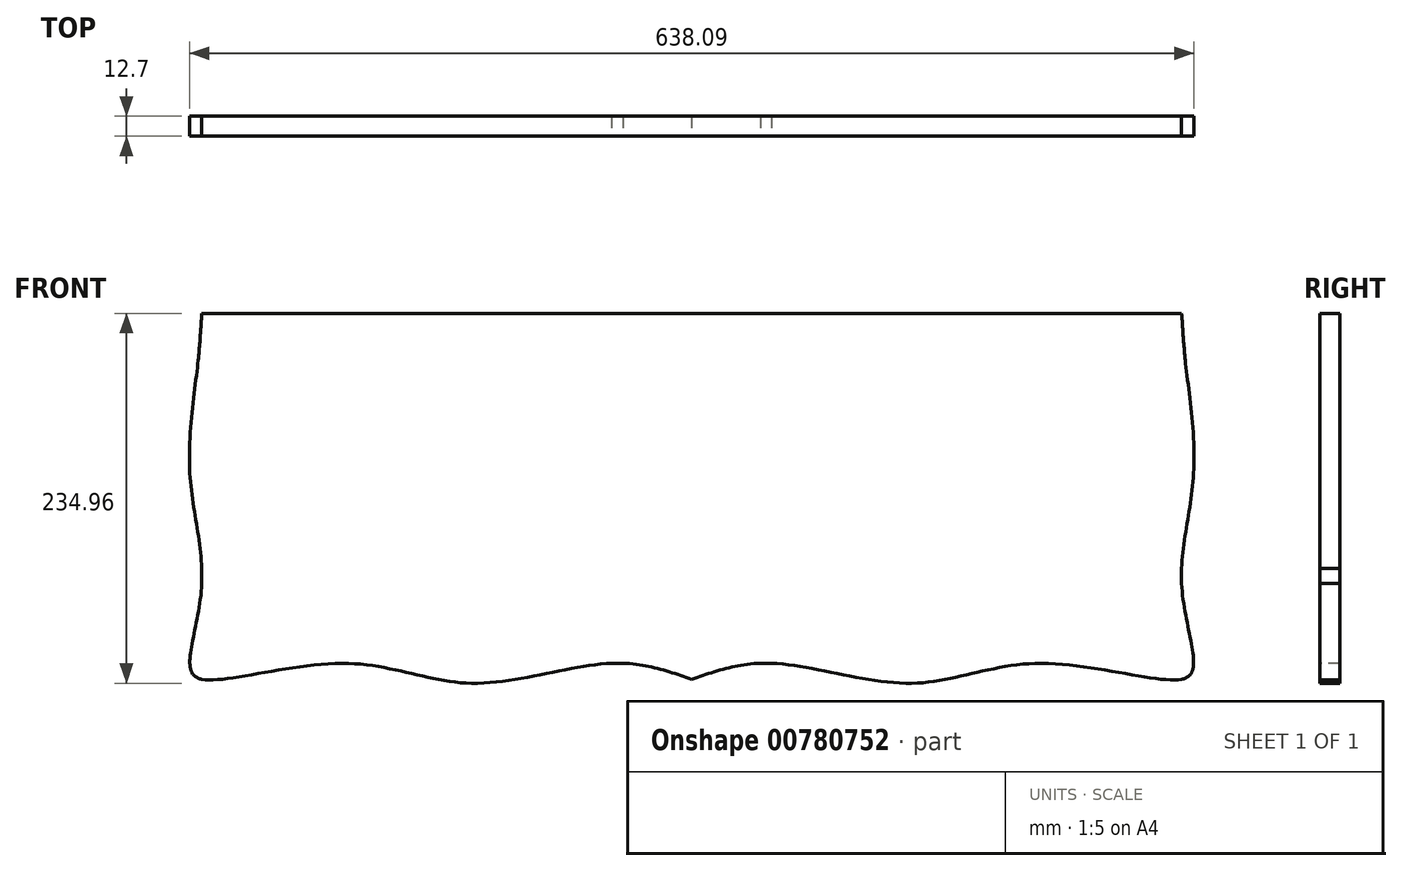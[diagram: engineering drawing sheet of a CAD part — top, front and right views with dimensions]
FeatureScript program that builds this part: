
annotation { "Feature Type Name" : "Feature", "Feature Type Description" : "" }
export const myFeature = defineFeature(function(context is Context, id is Id, definition is map)
    precondition{}
    {
        {
            var Q0;
            Q0=qCreatedBy(makeId("Front.planeOp"),FACE);
            var sketch = newSketch(context, id + "F0", { "sketchPlane" : qUnion([Q0])});
            skLineSegment(sketch, "E0.bottom", {"start": v(-290.57, 108.48) * mm, "end": v(331.73, 108.48) * mm});
            skLineSegment(sketch, "E0.top", {"start": v(-290.57, -113.77) * mm, "end": v(331.73, -113.77) * mm});
            skLineSegment(sketch, "E0.left", {"start": v(-290.57, 108.48) * mm, "end": v(-290.57, -113.77) * mm});
            skLineSegment(sketch, "E0.right", {"start": v(331.73, 108.48) * mm, "end": v(331.73, -113.77) * mm});
            skPoint(sketch, "E1", {"position": v(20.58, 108.48) * mm});
            skSolve(sketch);
        }
        {
            var Q0;
            Q0=makeQuery(id+"F0.imprint","IMPRINT",FACE,{"disambiguationData":[TD([[makeQuery(id+"F0.imprint","IMPRINT",EDGE,{"derivedFrom":sQuery(id+"F0.wireOp",EDGE,"E0.bottom")}),-1.0]])]});
            extrude(context, id + "F1", {"entities" : qUnion([Q0]), "depth" : 12.7 * mm, "offsetDistance" : 25.4 * mm});
        }
        {
            var Q0;
            {var subQ0=sQuery(id+"F0.wireOp",EDGE,"E0.right");var subQ1=sQuery(id+"F0.wireOp",EDGE,"E0.bottom");var subQ2=sQuery(id+"F0.wireOp",EDGE,"E0.left");var subQ3=sQuery(id+"F0.wireOp",EDGE,"E0.top");Q0=makeQuery(id+"FjgwLtvUwF4HY63_1.boolean.opBoolean","SPLIT",FACE,{"disambiguationData":[TD([makeQuery(id+"F1.opExtrude","SWEPT_FACE",FACE,{"disambiguationData":[OSD([subQ1])]})])],"derivedFrom":makeQuery(id+"F1.opExtrude","CAP_FACE",FACE,{"disambiguationData":[OSD([subQ1,subQ3,subQ2,subQ0])],"isStart":false})});}
            var sketch = newSketch(context, id + "F2", { "sketchPlane" : qUnion([Q0])});
            skPoint(sketch, "E2", {"position": v(-290.57, -62.97) * mm});
            skPoint(sketch, "E3", {"position": v(-290.57, 6.88) * mm});
            skPoint(sketch, "E4", {"position": v(-290.57, 76.73) * mm});
            skLineSegment(sketch, "E5", {"start": v(-290.57, 76.73) * mm, "end": v(-293.1, 76.73) * mm});
            skLineSegment(sketch, "E6", {"start": v(-290.57, 6.88) * mm, "end": v(-298.19, 6.88) * mm});
            skLineSegment(sketch, "E7", {"start": v(-290.57, -113.77) * mm, "end": v(-298.19, -113.77) * mm});
            skLineSegment(sketch, "E8", {"start": v(-290.57, -113.77) * mm, "end": v(-290.57, -123.93) * mm});
            skPoint(sketch, "E9", {"position": v(-201.67, -113.77) * mm});
            skPoint(sketch, "E10", {"position": v(20.58, -113.77) * mm});
            skPoint(sketch, "E11", {"position": v(-30.22, -113.77) * mm});
            skPoint(sketch, "E12", {"position": v(-119.12, -113.77) * mm});
            skPoint(sketch, "E13", {"position": v(71.38, -113.77) * mm});
            skPoint(sketch, "E14", {"position": v(160.28, -113.77) * mm});
            skPoint(sketch, "E15", {"position": v(242.83, -113.77) * mm});
            skPoint(sketch, "E16", {"position": v(331.73, -62.97) * mm});
            skPoint(sketch, "E17", {"position": v(331.73, 6.88) * mm});
            skPoint(sketch, "E18", {"position": v(331.73, 76.73) * mm});
            skLineSegment(sketch, "E19", {"start": v(331.73, 76.73) * mm, "end": v(334.27, 76.73) * mm});
            skLineSegment(sketch, "E20", {"start": v(331.73, 6.88) * mm, "end": v(339.35, 6.88) * mm});
            skLineSegment(sketch, "E21", {"start": v(331.73, -113.77) * mm, "end": v(339.35, -113.77) * mm});
            skLineSegment(sketch, "E22", {"start": v(331.73, -113.77) * mm, "end": v(331.73, -123.93) * mm});
            skLineSegment(sketch, "E23", {"start": v(-119.12, -113.77) * mm, "end": v(-119.12, -126.47) * mm});
            skLineSegment(sketch, "E24", {"start": v(20.58, -113.77) * mm, "end": v(20.58, -123.93) * mm});
            skLineSegment(sketch, "E25", {"start": v(160.28, -113.77) * mm, "end": v(160.28, -126.47) * mm});
            skFitSpline(sketch, "E26", {"points": [v(-290.57, 108.48) * mm, v(-293.1, 76.73) * mm, v(-298.19, 6.88) * mm, v(-290.57, -62.97) * mm, v(-298.19, -113.77) * mm, v(-290.57, -123.93) * mm, v(-201.67, -113.77) * mm, v(-119.12, -126.47) * mm, v(-30.22, -113.77) * mm, v(20.58, -123.93) * mm], "startDerivative": vector(-26.2, -341.82) * mm, "endDerivative": vector(438.15, -148.5) * mm});
            skFitSpline(sketch, "E27", {"points": [v(331.73, 108.48) * mm, v(334.27, 76.73) * mm, v(339.35, 6.88) * mm, v(331.73, -62.97) * mm, v(339.35, -113.77) * mm, v(331.73, -123.93) * mm, v(242.83, -113.77) * mm, v(160.28, -126.47) * mm, v(71.38, -113.77) * mm, v(20.58, -123.93) * mm], "startDerivative": vector(26.2, -341.82) * mm, "endDerivative": vector(-438.15, -148.5) * mm});
            skSolve(sketch);
        }
        {
            var Q0;
            {var subQ0=sQuery(id+"F2.wireOp",EDGE,"E24");Q0=makeQuery(id+"F2.imprint","IMPRINT",FACE,{"disambiguationData":[TD([[makeQuery(id+"F2.imprint","IMPRINT",EDGE,{"derivedFrom":subQ0}),-1.0]])]});}
            var Q1;
            {var subQ0=sQuery(id+"F2.wireOp",EDGE,"E24");Q1=makeQuery(id+"F2.imprint","IMPRINT",FACE,{"disambiguationData":[TD([[makeQuery(id+"F2.imprint","IMPRINT",EDGE,{"derivedFrom":subQ0}),1.0]])]});}
            var Q2;
            {var subQ0=sQuery(id+"F2.wireOp",EDGE,"E23");Q2=makeQuery(id+"F2.imprint","IMPRINT",FACE,{"disambiguationData":[TD([[makeQuery(id+"F2.imprint","IMPRINT",EDGE,{"derivedFrom":subQ0}),1.0]])]});}
            var Q3;
            {var subQ0=sQuery(id+"F2.wireOp",EDGE,"E23");Q3=makeQuery(id+"F2.imprint","IMPRINT",FACE,{"disambiguationData":[TD([[makeQuery(id+"F2.imprint","IMPRINT",EDGE,{"derivedFrom":subQ0}),-1.0]])]});}
            var Q4;
            {var subQ0=sQuery(id+"F2.wireOp",EDGE,"E8");Q4=makeQuery(id+"F2.imprint","IMPRINT",FACE,{"disambiguationData":[TD([[makeQuery(id+"F2.imprint","IMPRINT",EDGE,{"derivedFrom":subQ0}),1.0]])]});}
            var Q5;
            {var subQ0=sQuery(id+"F2.wireOp",EDGE,"E7");Q5=makeQuery(id+"F2.imprint","IMPRINT",FACE,{"disambiguationData":[TD([[makeQuery(id+"F2.imprint","IMPRINT",EDGE,{"derivedFrom":subQ0}),1.0]])]});}
            var Q6;
            {var subQ0=sQuery(id+"F2.wireOp",EDGE,"E7");Q6=makeQuery(id+"F2.imprint","IMPRINT",FACE,{"disambiguationData":[TD([[makeQuery(id+"F2.imprint","IMPRINT",EDGE,{"derivedFrom":subQ0}),-1.0]])]});}
            var Q7;
            {var subQ0=sQuery(id+"F2.wireOp",EDGE,"E6");Q7=makeQuery(id+"F2.imprint","IMPRINT",FACE,{"disambiguationData":[TD([[makeQuery(id+"F2.imprint","IMPRINT",EDGE,{"derivedFrom":subQ0}),1.0]])]});}
            var Q8;
            {var subQ0=sQuery(id+"F2.wireOp",EDGE,"E5");Q8=makeQuery(id+"F2.imprint","IMPRINT",FACE,{"disambiguationData":[TD([[makeQuery(id+"F2.imprint","IMPRINT",EDGE,{"derivedFrom":subQ0}),1.0]])]});}
            var Q9;
            {var subQ0=makeQuery(id+"F1.opExtrude","CAP_EDGE",EDGE,{"disambiguationData":[OSD([sQuery(id+"F0.wireOp",EDGE,"E0.bottom")])],"isStart":false});Q9=makeQuery(id+"F2.imprint","IMPRINT",FACE,{"disambiguationData":[TD([[makeQuery(id+"F2.imprint","IMPRINT",EDGE,{"derivedFrom":subQ0}),-1.0]])]});}
            var Q10;
            {var subQ0=sQuery(id+"F2.wireOp",EDGE,"E25");Q10=makeQuery(id+"F2.imprint","IMPRINT",FACE,{"disambiguationData":[TD([[makeQuery(id+"F2.imprint","IMPRINT",EDGE,{"derivedFrom":subQ0}),-1.0]])]});}
            var Q11;
            {var subQ0=sQuery(id+"F2.wireOp",EDGE,"E25");Q11=makeQuery(id+"F2.imprint","IMPRINT",FACE,{"disambiguationData":[TD([[makeQuery(id+"F2.imprint","IMPRINT",EDGE,{"derivedFrom":subQ0}),1.0]])]});}
            var Q12;
            {var subQ0=sQuery(id+"F2.wireOp",EDGE,"E22");Q12=makeQuery(id+"F2.imprint","IMPRINT",FACE,{"disambiguationData":[TD([[makeQuery(id+"F2.imprint","IMPRINT",EDGE,{"derivedFrom":subQ0}),-1.0]])]});}
            var Q13;
            {var subQ0=sQuery(id+"F2.wireOp",EDGE,"E21");Q13=makeQuery(id+"F2.imprint","IMPRINT",FACE,{"disambiguationData":[TD([[makeQuery(id+"F2.imprint","IMPRINT",EDGE,{"derivedFrom":subQ0}),-1.0]])]});}
            var Q14;
            {var subQ0=sQuery(id+"F2.wireOp",EDGE,"E21");Q14=makeQuery(id+"F2.imprint","IMPRINT",FACE,{"disambiguationData":[TD([[makeQuery(id+"F2.imprint","IMPRINT",EDGE,{"derivedFrom":subQ0}),1.0]])]});}
            var Q15;
            {var subQ0=sQuery(id+"F2.wireOp",EDGE,"E20");Q15=makeQuery(id+"F2.imprint","IMPRINT",FACE,{"disambiguationData":[TD([[makeQuery(id+"F2.imprint","IMPRINT",EDGE,{"derivedFrom":subQ0}),-1.0]])]});}
            var Q16;
            {var subQ0=sQuery(id+"F2.wireOp",EDGE,"E19");Q16=makeQuery(id+"F2.imprint","IMPRINT",FACE,{"disambiguationData":[TD([[makeQuery(id+"F2.imprint","IMPRINT",EDGE,{"derivedFrom":subQ0}),-1.0]])]});}
            var Q17;
            {var subQ0=sQuery(id+"F2.wireOp",EDGE,"E19");Q17=makeQuery(id+"F2.imprint","IMPRINT",FACE,{"disambiguationData":[TD([[makeQuery(id+"F2.imprint","IMPRINT",EDGE,{"derivedFrom":subQ0}),1.0]])]});}
            var Q18;
            {var subQ0=sQuery(id+"F2.wireOp",EDGE,"E5");Q18=makeQuery(id+"F2.imprint","IMPRINT",FACE,{"disambiguationData":[TD([[makeQuery(id+"F2.imprint","IMPRINT",EDGE,{"derivedFrom":subQ0}),-1.0]])]});}
            extrude(context, id + "F3", {"entities" : qUnion([Q0, Q1, Q2, Q3, Q4, Q5, Q6, Q7, Q8, Q9, Q10, Q11, Q12, Q13, Q14, Q15, Q16, Q17, Q18]), "operationType" : NewBodyOperationType.ADD, "depth" : -12.7 * mm, "offsetDistance" : 25.4 * mm});
        }
    });
